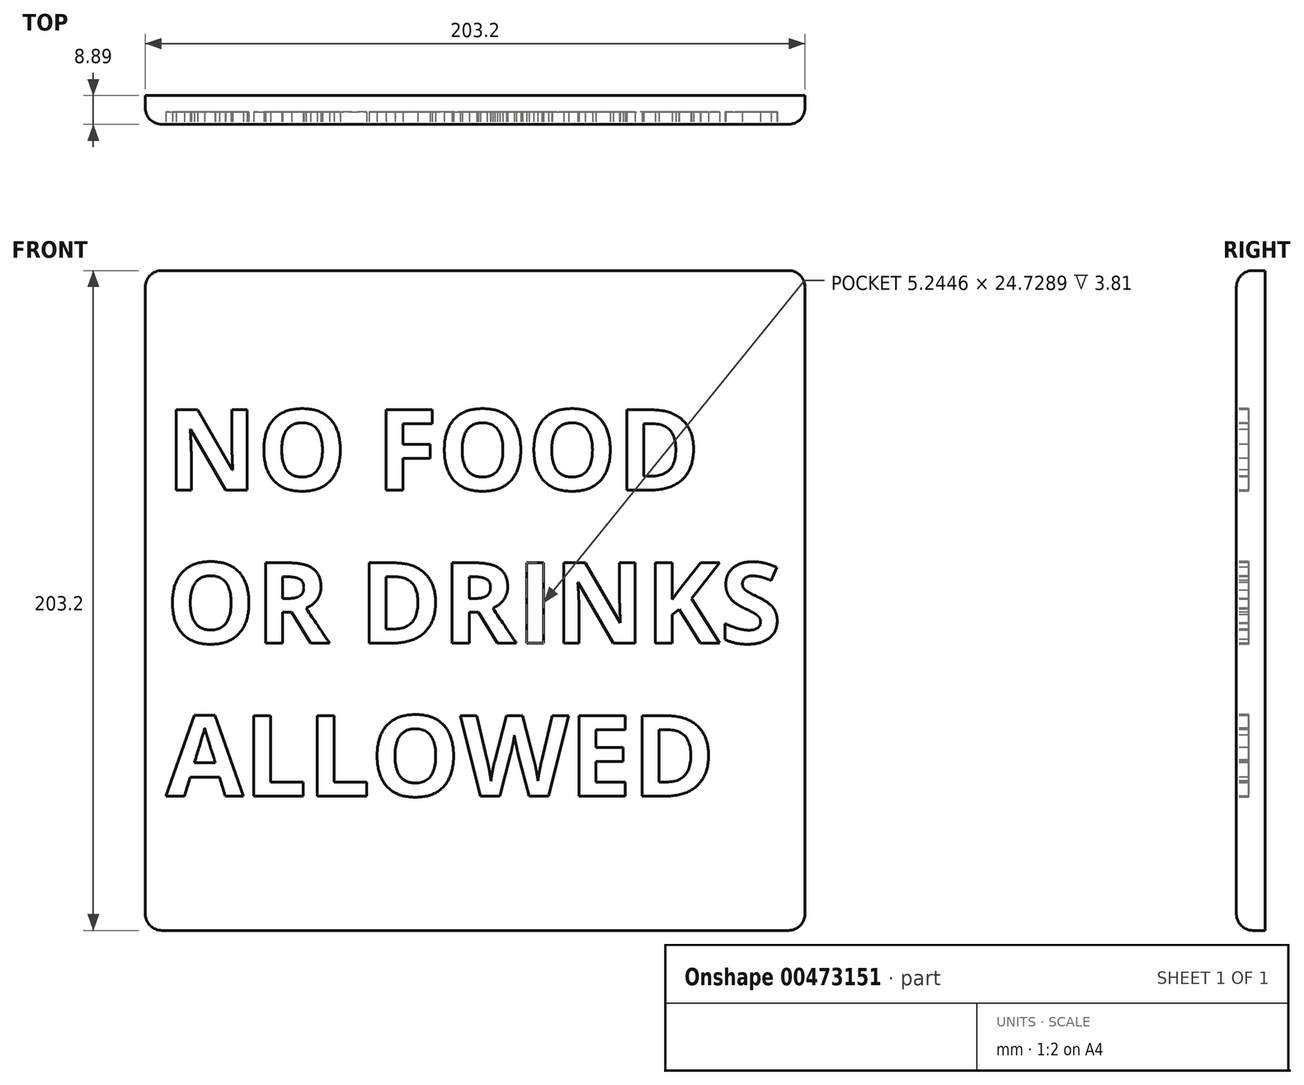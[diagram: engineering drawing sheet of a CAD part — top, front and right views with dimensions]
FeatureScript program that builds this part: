
annotation { "Feature Type Name" : "Feature", "Feature Type Description" : "" }
export const myFeature = defineFeature(function(context is Context, id is Id, definition is map)
    precondition{}
    {
        {
            var Q0;
            Q0=qCreatedBy(makeId("Front.planeOp"),FACE);
            var sketch = newSketch(context, id + "F0", { "sketchPlane" : qUnion([Q0])});
            skLineSegment(sketch, "E0.bottom", {"start": v(101.6, 101.6) * mm, "end": v(-101.6, 101.6) * mm});
            skLineSegment(sketch, "E0.top", {"start": v(101.6, -101.6) * mm, "end": v(-101.6, -101.6) * mm});
            skLineSegment(sketch, "E0.left", {"start": v(101.6, 101.6) * mm, "end": v(101.6, -101.6) * mm});
            skLineSegment(sketch, "E0.right", {"start": v(-101.6, 101.6) * mm, "end": v(-101.6, -101.6) * mm});
            skPoint(sketch, "E0.middle", {"position": v(0, 0) * mm});
            skSolve(sketch);
        }
        {
            var Q0;
            Q0 = qSketchRegion(id + "F0", true);
            extrude(context, id + "F1", {"entities" : qUnion([Q0]), "depth" : 8.9 * mm, "offsetDistance" : 25.4 * mm});
        }
        {
            var Q0;
            Q0=makeQuery(id+"F1.opExtrude","CAP_FACE",FACE,{"disambiguationData":[OSD([sQuery(id+"F0.wireOp",EDGE,"E0.bottom"),sQuery(id+"F0.wireOp",EDGE,"E0.top"),sQuery(id+"F0.wireOp",EDGE,"E0.left"),sQuery(id+"F0.wireOp",EDGE,"E0.right")])],"isStart":false});
            var sketch = newSketch(context, id + "F2", { "sketchPlane" : qUnion([Q0])});
            skText(sketch, "E1", { "text": "NO FOOD \nOR DRINKS\nALLOWED", "fontName": "OpenSans-Bold.ttf"});
            const initialGuessF2  = {"E1": [-0.09525, 0.03397, 1, 0, 0.02494]};
            skSetInitialGuess(sketch, initialGuessF2);
            skSolve(sketch);
        }
        {
            var Q0;
            Q0 = qSketchRegion(id + "F2", true);
            extrude(context, id + "F3", {"entities" : qUnion([Q0]), "operationType" : NewBodyOperationType.REMOVE, "oppositeDirection" : true, "depth" : 3.8 * mm});
        }
        {
            var Q0;
            Q0=makeQuery(id+"F1.opExtrude","CAP_EDGE",EDGE,{"disambiguationData":[OSD([sQuery(id+"F0.wireOp",EDGE,"E0.bottom")])],"isStart":false});
            var Q1;
            Q1=makeQuery(id+"F1.opExtrude","CAP_EDGE",EDGE,{"disambiguationData":[OSD([sQuery(id+"F0.wireOp",EDGE,"E0.right")])],"isStart":false});
            var Q2;
            Q2=makeQuery(id+"F1.opExtrude","CAP_EDGE",EDGE,{"disambiguationData":[OSD([sQuery(id+"F0.wireOp",EDGE,"E0.top")])],"isStart":false});
            var Q3;
            Q3=makeQuery(id+"F1.opExtrude","CAP_EDGE",EDGE,{"disambiguationData":[OSD([sQuery(id+"F0.wireOp",EDGE,"E0.left")])],"isStart":false});
            fillet(context, id + "F4", {"entities" : qUnion([Q0, Q1, Q2, Q3]), "radius" : 5.08 * mm, "tangentPropagation" : true, "allowEdgeOverflow" : false});
        }
        {
            var Q0;
            Q0=makeQuery(id+"F4.opFillet","BLEND_EDGE",EDGE,{"blendedFrom":[makeQuery(id+"F1.opExtrude","CAP_EDGE",EDGE,{"disambiguationData":[OSD([sQuery(id+"F0.wireOp",EDGE,"E0.bottom")])],"isStart":false}),makeQuery(id+"F1.opExtrude","CAP_EDGE",EDGE,{"disambiguationData":[OSD([sQuery(id+"F0.wireOp",EDGE,"E0.left")])],"isStart":false})],"blendedInto":[]});
            fillet(context, id + "F5", {"entities" : qUnion([Q0]), "radius" : 5.08 * mm, "tangentPropagation" : true, "allowEdgeOverflow" : false});
        }
        {
            var Q0;
            Q0=makeQuery(id+"F4.opFillet","BLEND_EDGE",EDGE,{"blendedFrom":[makeQuery(id+"F1.opExtrude","CAP_EDGE",EDGE,{"disambiguationData":[OSD([sQuery(id+"F0.wireOp",EDGE,"E0.bottom")])],"isStart":false}),makeQuery(id+"F1.opExtrude","CAP_EDGE",EDGE,{"disambiguationData":[OSD([sQuery(id+"F0.wireOp",EDGE,"E0.right")])],"isStart":false})],"blendedInto":[]});
            var Q1;
            Q1=makeQuery(id+"F4.opFillet","BLEND_EDGE",EDGE,{"blendedFrom":[makeQuery(id+"F1.opExtrude","CAP_EDGE",EDGE,{"disambiguationData":[OSD([sQuery(id+"F0.wireOp",EDGE,"E0.top")])],"isStart":false}),makeQuery(id+"F1.opExtrude","CAP_EDGE",EDGE,{"disambiguationData":[OSD([sQuery(id+"F0.wireOp",EDGE,"E0.right")])],"isStart":false})],"blendedInto":[]});
            var Q2;
            Q2=makeQuery(id+"F4.opFillet","BLEND_EDGE",EDGE,{"blendedFrom":[makeQuery(id+"F1.opExtrude","CAP_EDGE",EDGE,{"disambiguationData":[OSD([sQuery(id+"F0.wireOp",EDGE,"E0.top")])],"isStart":false}),makeQuery(id+"F1.opExtrude","CAP_EDGE",EDGE,{"disambiguationData":[OSD([sQuery(id+"F0.wireOp",EDGE,"E0.left")])],"isStart":false})],"blendedInto":[]});
            fillet(context, id + "F6", {"entities" : qUnion([Q0, Q1, Q2]), "radius" : 5.08 * mm, "tangentPropagation" : true, "allowEdgeOverflow" : false});
        }
    });
